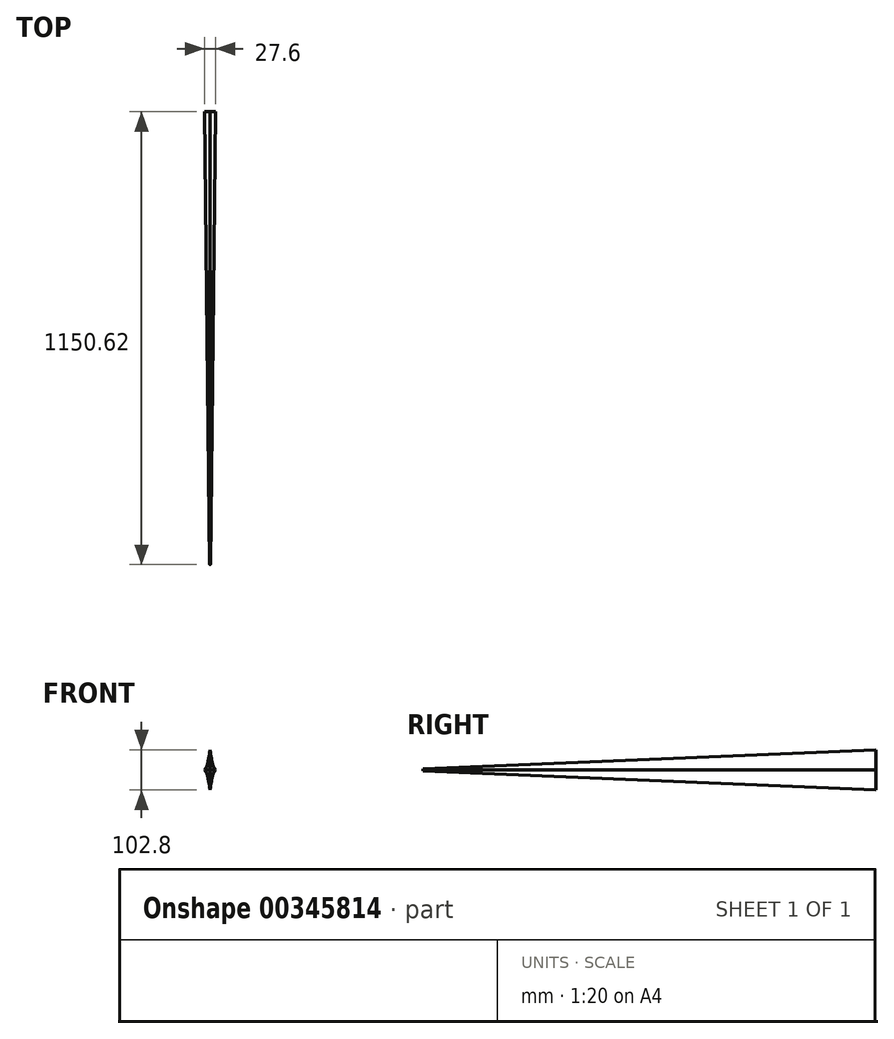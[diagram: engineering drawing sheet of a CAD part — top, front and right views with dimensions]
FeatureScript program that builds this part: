
annotation { "Feature Type Name" : "Feature", "Feature Type Description" : "" }
export const myFeature = defineFeature(function(context is Context, id is Id, definition is map)
    precondition{}
    {
        {
            var Q0;
            Q0=qCreatedBy(makeId("Front.planeOp"),FACE);
            var sketch = newSketch(context, id + "F0", { "sketchPlane" : qUnion([Q0])});
            skFitSpline(sketch, "E0", {"points": [v(0, 51.4) * mm, v(7.93, 10.28) * mm, v(13.8, 0) * mm], "startDerivative": vector(10.59, -73.87) * mm, "endDerivative": vector(17.75, -23.82) * mm});
            skFitSpline(sketch, "E1.MirrorCS", {"points": [v(0, 51.4) * mm, v(-7.93, 10.28) * mm, v(-13.8, 0) * mm], "startDerivative": vector(-10.59, -73.87) * mm, "endDerivative": vector(-17.75, -23.82) * mm});
            skFitSpline(sketch, "E2.MirrorCS", {"points": [v(0, -51.4) * mm, v(-7.93, -10.28) * mm, v(-13.8, 0) * mm], "startDerivative": vector(-10.59, 73.87) * mm, "endDerivative": vector(-17.75, 23.82) * mm});
            skFitSpline(sketch, "E3.MirrorCS", {"points": [v(0, -51.4) * mm, v(7.93, -10.28) * mm, v(13.8, 0) * mm], "startDerivative": vector(10.59, 73.87) * mm, "endDerivative": vector(17.75, 23.82) * mm});
            skSolve(sketch);
        }
        {
            var Q0;
            Q0=qCreatedBy(makeId("Front.planeOp"),FACE);
            cPlane(context, id + "F1", {"entities" : qUnion([Q0]), "cplaneType" : CPlaneType.OFFSET, "offset" : 1150.62 * mm, "width" : 152.4 * mm, "height" : 152.4 * mm});
        }
        {
            var Q0;
            Q0=qCreatedBy(id+"F1.planeOp",FACE);
            var sketch = newSketch(context, id + "F2", { "sketchPlane" : qUnion([Q0])});
            skFitSpline(sketch, "E4", {"points": [v(0, 2.15) * mm, v(0.31, 0.47) * mm, v(1.14, 0) * mm], "startDerivative": vector(0.14, -3.48) * mm, "endDerivative": vector(2.24, -0.7) * mm});
            skFitSpline(sketch, "E5.MirrorCS", {"points": [v(0, 2.15) * mm, v(-0.31, 0.47) * mm, v(-1.14, 0) * mm], "startDerivative": vector(-0.14, -3.48) * mm, "endDerivative": vector(-2.24, -0.7) * mm});
            skFitSpline(sketch, "E6.MirrorCS", {"points": [v(0, -2.15) * mm, v(-0.31, -0.47) * mm, v(-1.14, 0) * mm], "startDerivative": vector(-0.14, 3.48) * mm, "endDerivative": vector(-2.24, 0.7) * mm});
            skFitSpline(sketch, "E7.MirrorCS", {"points": [v(0, -2.15) * mm, v(0.31, -0.47) * mm, v(1.14, 0) * mm], "startDerivative": vector(0.14, 3.48) * mm, "endDerivative": vector(2.24, 0.7) * mm});
            skSolve(sketch);
        }
        {
            var Q0;
            Q0=makeQuery(id+"F0.imprint","IMPRINT",FACE,{"disambiguationData":[TD([[makeQuery(id+"F0.imprint","IMPRINT",EDGE,{"derivedFrom":sQuery(id+"F0.wireOp",EDGE,"E0")}),-1.0]])]});
            var Q1;
            Q1=makeQuery(id+"F2.imprint","IMPRINT",FACE,{"disambiguationData":[TD([[makeQuery(id+"F2.imprint","IMPRINT",EDGE,{"derivedFrom":sQuery(id+"F2.wireOp",EDGE,"E4")}),-1.0]])]});
            loft(context, id + "F3", {"sheetProfilesArray" : [{ "sheetProfileEntities" : qUnion([Q0]) }, { "sheetProfileEntities" : qUnion([Q1]) }]});
        }
    });
